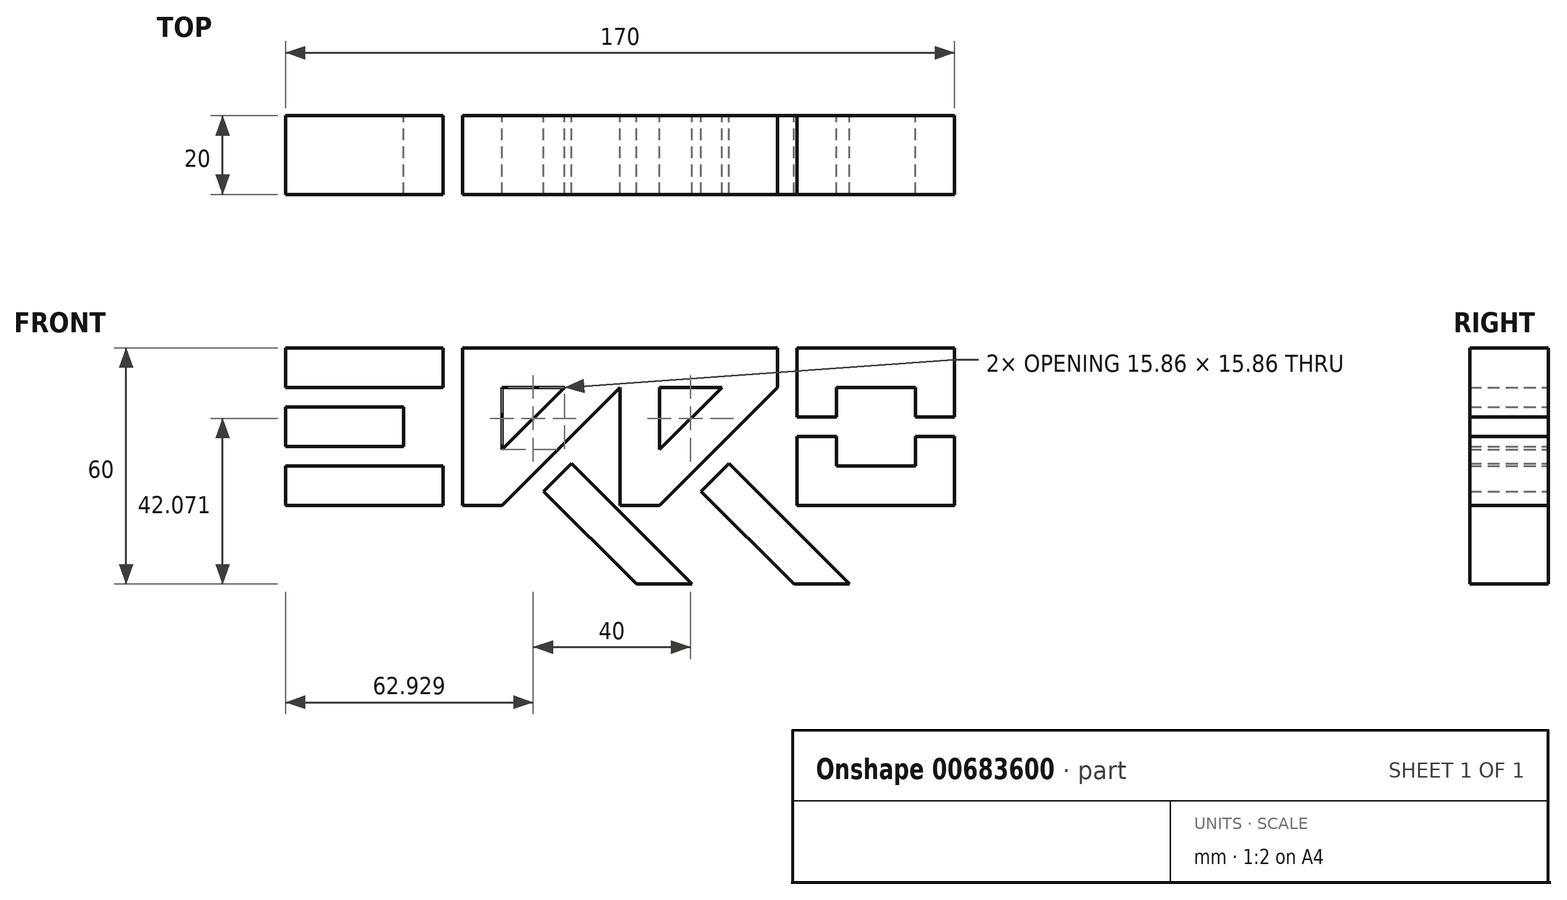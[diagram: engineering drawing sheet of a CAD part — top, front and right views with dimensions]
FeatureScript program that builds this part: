
annotation { "Feature Type Name" : "Feature", "Feature Type Description" : "" }
export const myFeature = defineFeature(function(context is Context, id is Id, definition is map)
    precondition{}
    {
        {
            var Q0;
            Q0=qCreatedBy(makeId("Front.planeOp"),FACE);
            var sketch = newSketch(context, id + "F0", { "sketchPlane" : qUnion([Q0])});
            skLineSegment(sketch, "E0.bottom", {"start": v(0, 0) * mm, "end": v(-40, 0) * mm});
            skLineSegment(sketch, "E0.top", {"start": v(0, 10) * mm, "end": v(-40, 10) * mm});
            skLineSegment(sketch, "E0.left", {"start": v(0, 0) * mm, "end": v(0, 10) * mm});
            skLineSegment(sketch, "E0.right", {"start": v(-40, 0) * mm, "end": v(-40, 10) * mm});
            skLineSegment(sketch, "E1.bottom", {"start": v(-40, 25) * mm, "end": v(-10, 25) * mm});
            skLineSegment(sketch, "E1.top", {"start": v(-40, 15) * mm, "end": v(-10, 15) * mm});
            skLineSegment(sketch, "E1.left", {"start": v(-40, 25) * mm, "end": v(-40, 15) * mm});
            skLineSegment(sketch, "E1.right", {"start": v(-10, 25) * mm, "end": v(-10, 15) * mm});
            skLineSegment(sketch, "E2.bottom", {"start": v(-40, 30) * mm, "end": v(0, 30) * mm});
            skLineSegment(sketch, "E2.top", {"start": v(-40, 40) * mm, "end": v(0, 40) * mm});
            skLineSegment(sketch, "E2.left", {"start": v(-40, 30) * mm, "end": v(-40, 40) * mm});
            skLineSegment(sketch, "E2.right", {"start": v(0, 30) * mm, "end": v(0, 40) * mm});
            skLineSegment(sketch, "E3", {"start": v(5, 0) * mm, "end": v(5, 40) * mm});
            skLineSegment(sketch, "E4", {"start": v(5, 40) * mm, "end": v(45, 40) * mm});
            skLineSegment(sketch, "E5", {"start": v(45, 40) * mm, "end": v(45, 30) * mm});
            skLineSegment(sketch, "E6", {"start": v(15, 0) * mm, "end": v(5, 0) * mm});
            skLineSegment(sketch, "E7", {"start": v(45, 30) * mm, "end": v(29.14, 14.14) * mm});
            skLineSegment(sketch, "E8", {"start": v(15, 0) * mm, "end": v(15, 0) * mm});
            skLineSegment(sketch, "E9", {"start": v(15, 30) * mm, "end": v(30.86, 30) * mm});
            skLineSegment(sketch, "E10", {"start": v(30.86, 30) * mm, "end": v(15, 14.14) * mm});
            skLineSegment(sketch, "E11", {"start": v(15, 14.14) * mm, "end": v(15, 30) * mm});
            skLineSegment(sketch, "E12", {"start": v(25.6, 3.54) * mm, "end": v(49.14, -20) * mm});
            skLineSegment(sketch, "E13", {"start": v(63.28, -20) * mm, "end": v(32.68, 10.6) * mm});
            skLineSegment(sketch, "E14", {"start": v(15, 14.14) * mm, "end": v(22.07, 7.07) * mm, "construction": true});
            skLineSegment(sketch, "E15.trimOffspring", {"start": v(22.07, 7.07) * mm, "end": v(15, 0) * mm});
            skLineSegment(sketch, "E16", {"start": v(45, 0) * mm, "end": v(45, 40) * mm});
            skLineSegment(sketch, "E17", {"start": v(45, 40) * mm, "end": v(85, 40) * mm});
            skLineSegment(sketch, "E18", {"start": v(85, 40) * mm, "end": v(85, 30) * mm});
            skLineSegment(sketch, "E19", {"start": v(55, 0) * mm, "end": v(45, 0) * mm});
            skLineSegment(sketch, "E20", {"start": v(85, 30) * mm, "end": v(69.14, 14.14) * mm});
            skLineSegment(sketch, "E21", {"start": v(55, 30) * mm, "end": v(70.86, 30) * mm});
            skLineSegment(sketch, "E22", {"start": v(70.86, 30) * mm, "end": v(55, 14.14) * mm});
            skLineSegment(sketch, "E23", {"start": v(55, 14.14) * mm, "end": v(55, 30) * mm});
            skLineSegment(sketch, "E24", {"start": v(65.6, 3.54) * mm, "end": v(89.14, -20) * mm});
            skLineSegment(sketch, "E25", {"start": v(103.28, -20) * mm, "end": v(72.68, 10.6) * mm});
            skLineSegment(sketch, "E26", {"start": v(55, 14.14) * mm, "end": v(62.07, 7.07) * mm, "construction": true});
            skLineSegment(sketch, "E27.trimOffspring", {"start": v(62.07, 7.07) * mm, "end": v(55, 0) * mm});
            skLineSegment(sketch, "E28.bottom", {"start": v(90, 0) * mm, "end": v(130, 0) * mm});
            skLineSegment(sketch, "E28.top", {"start": v(90, 40) * mm, "end": v(130, 40) * mm});
            skLineSegment(sketch, "E28.left", {"start": v(90, 0) * mm, "end": v(90, 17.5) * mm});
            skLineSegment(sketch, "E28.right", {"start": v(130, 0) * mm, "end": v(130, 17.5) * mm});
            skLineSegment(sketch, "E29.bottom", {"start": v(100, 30) * mm, "end": v(120, 30) * mm});
            skLineSegment(sketch, "E29.top", {"start": v(100, 10) * mm, "end": v(120, 10) * mm});
            skLineSegment(sketch, "E29.left", {"start": v(100, 30) * mm, "end": v(100, 22.5) * mm});
            skLineSegment(sketch, "E29.right", {"start": v(120, 30) * mm, "end": v(120, 22.5) * mm});
            skLineSegment(sketch, "E30", {"start": v(90, 17.5) * mm, "end": v(100, 17.5) * mm});
            skLineSegment(sketch, "E31", {"start": v(100, 22.5) * mm, "end": v(90, 22.5) * mm});
            skLineSegment(sketch, "E32", {"start": v(120, 22.5) * mm, "end": v(130, 22.5) * mm});
            skLineSegment(sketch, "E33", {"start": v(120, 17.5) * mm, "end": v(130, 17.5) * mm});
            skLineSegment(sketch, "E34.trimOffspring", {"start": v(90, 22.5) * mm, "end": v(90, 40) * mm});
            skLineSegment(sketch, "E35.trimOffspring", {"start": v(100, 17.5) * mm, "end": v(100, 10) * mm});
            skLineSegment(sketch, "E36.trimOffspring", {"start": v(120, 17.5) * mm, "end": v(120, 10) * mm});
            skLineSegment(sketch, "E37.trimOffspring", {"start": v(130, 22.5) * mm, "end": v(130, 40) * mm});
            skLineSegment(sketch, "E38", {"start": v(22.07, 7.07) * mm, "end": v(29.14, 14.14) * mm});
            skLineSegment(sketch, "E39", {"start": v(62.07, 7.07) * mm, "end": v(69.14, 14.14) * mm});
            skLineSegment(sketch, "E40", {"start": v(25.6, 3.54) * mm, "end": v(32.68, 10.6) * mm});
            skLineSegment(sketch, "E41", {"start": v(65.6, 3.54) * mm, "end": v(72.68, 10.6) * mm});
            skLineSegment(sketch, "E42", {"start": v(49.14, -20) * mm, "end": v(63.28, -20) * mm});
            skLineSegment(sketch, "E43.trimOffspring", {"start": v(89.14, -20) * mm, "end": v(103.28, -20) * mm});
            skSolve(sketch);
        }
        {
            var Q0;
            Q0=makeQuery(id+"F0.imprint","IMPRINT",FACE,{"disambiguationData":[TD([[makeQuery(id+"F0.imprint","IMPRINT",EDGE,{"derivedFrom":sQuery(id+"F0.wireOp",EDGE,"E1.bottom")}),-1.0]])]});
            var Q1;
            Q1=makeQuery(id+"F0.imprint","IMPRINT",FACE,{"disambiguationData":[TD([[makeQuery(id+"F0.imprint","IMPRINT",EDGE,{"derivedFrom":sQuery(id+"F0.wireOp",EDGE,"E2.bottom")}),1.0]])]});
            var Q2;
            Q2=makeQuery(id+"F0.imprint","IMPRINT",FACE,{"disambiguationData":[TD([[makeQuery(id+"F0.imprint","IMPRINT",EDGE,{"derivedFrom":sQuery(id+"F0.wireOp",EDGE,"E0.bottom")}),-1.0]])]});
            var Q3;
            Q3=makeQuery(id+"F0.imprint","IMPRINT",FACE,{"disambiguationData":[TD([[makeQuery(id+"F0.imprint","IMPRINT",EDGE,{"derivedFrom":sQuery(id+"F0.wireOp",EDGE,"E3")}),-1.0]])]});
            var Q4;
            Q4=makeQuery(id+"F0.imprint","IMPRINT",FACE,{"disambiguationData":[TD([[makeQuery(id+"F0.imprint","IMPRINT",EDGE,{"derivedFrom":sQuery(id+"F0.wireOp",EDGE,"E12")}),1.0]])]});
            var Q5;
            Q5=makeQuery(id+"F0.imprint","IMPRINT",FACE,{"disambiguationData":[TD([[makeQuery(id+"F0.imprint","IMPRINT",EDGE,{"derivedFrom":sQuery(id+"F0.wireOp",EDGE,"E24")}),1.0]])]});
            var Q6;
            Q6=makeQuery(id+"F0.imprint","IMPRINT",FACE,{"disambiguationData":[TD([[makeQuery(id+"F0.imprint","IMPRINT",EDGE,{"derivedFrom":sQuery(id+"F0.wireOp",EDGE,"E16")}),-1.0]])]});
            var Q7;
            Q7=makeQuery(id+"F0.imprint","IMPRINT",FACE,{"disambiguationData":[TD([[makeQuery(id+"F0.imprint","IMPRINT",EDGE,{"derivedFrom":sQuery(id+"F0.wireOp",EDGE,"E28.top")}),-1.0]])]});
            var Q8;
            Q8=makeQuery(id+"F0.imprint","IMPRINT",FACE,{"disambiguationData":[TD([[makeQuery(id+"F0.imprint","IMPRINT",EDGE,{"derivedFrom":sQuery(id+"F0.wireOp",EDGE,"E28.bottom")}),1.0]])]});
            extrude(context, id + "F1", {"entities" : qUnion([Q0, Q1, Q2, Q3, Q4, Q5, Q6, Q7, Q8]), "depth" : 20 * mm, "offsetDistance" : 25 * mm});
        }
    });
